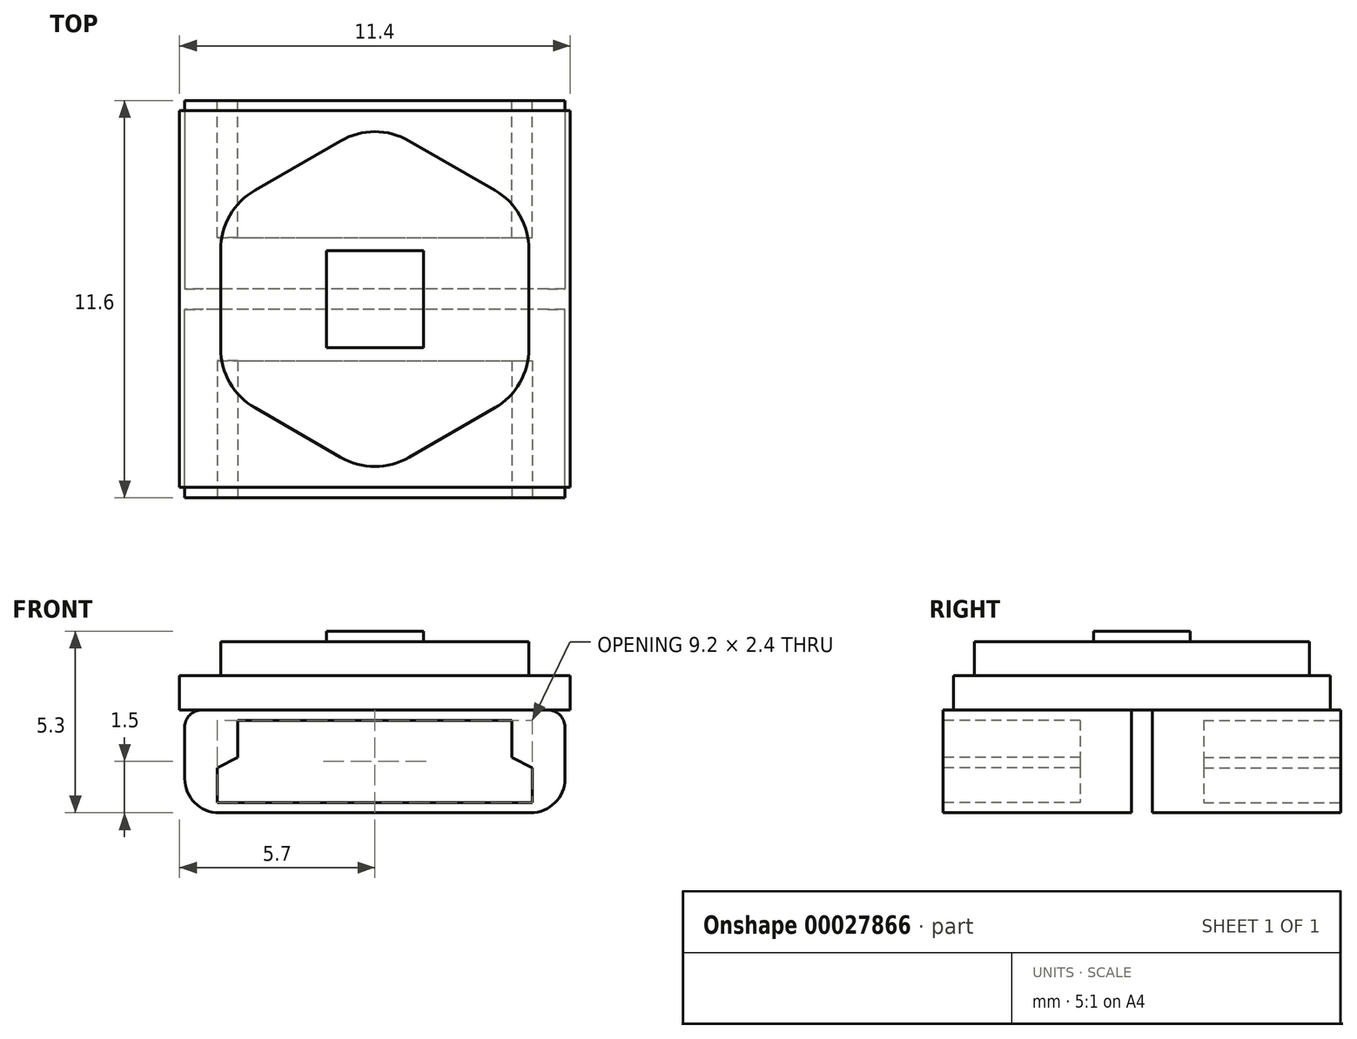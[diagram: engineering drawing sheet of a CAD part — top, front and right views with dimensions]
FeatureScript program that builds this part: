
annotation { "Feature Type Name" : "Feature", "Feature Type Description" : "" }
export const myFeature = defineFeature(function(context is Context, id is Id, definition is map)
    precondition{}
    {
        {
            var Q0;
            Q0=qCreatedBy(makeId("Top.planeOp"),FACE);
            var sketch = newSketch(context, id + "F0", { "sketchPlane" : qUnion([Q0])});
            skLineSegment(sketch, "E0.rect.bottom", {"start": v(6, -6) * mm, "end": v(-6, -6) * mm});
            skLineSegment(sketch, "E0.rect.top", {"start": v(6, 6) * mm, "end": v(-6, 6) * mm});
            skLineSegment(sketch, "E0.rect.left", {"start": v(6, -6) * mm, "end": v(6, 6) * mm});
            skLineSegment(sketch, "E0.rect.right", {"start": v(-6, -6) * mm, "end": v(-6, 6) * mm});
            skPoint(sketch, "E0.rect.middle", {"position": v(0, 0) * mm});
            skCircle(sketch, "E1", {"center": v(0, 0) * mm, "radius": 1.5 * mm});
            skSolve(sketch);
        }
        {
            var Q0;
            Q0=qCreatedBy(makeId("Front.planeOp"),FACE);
            var sketch = newSketch(context, id + "F1", { "sketchPlane" : qUnion([Q0])});
            skLineSegment(sketch, "E2.rect.bottom", {"start": v(6, -6) * mm, "end": v(-6, -6) * mm});
            skLineSegment(sketch, "E2.rect.top", {"start": v(6, 6) * mm, "end": v(-6, 6) * mm});
            skLineSegment(sketch, "E2.rect.left", {"start": v(6, -6) * mm, "end": v(6, 6) * mm});
            skLineSegment(sketch, "E2.rect.right", {"start": v(-6, -6) * mm, "end": v(-6, 6) * mm});
            skPoint(sketch, "E2.rect.middle", {"position": v(0, 0) * mm});
            skCircle(sketch, "E3", {"center": v(0, 0) * mm, "radius": 1.5 * mm});
            skSolve(sketch);
        }
        {
            var Q0;
            Q0=qCreatedBy(makeId("Right.planeOp"),FACE);
            var sketch = newSketch(context, id + "F2", { "sketchPlane" : qUnion([Q0])});
            skLineSegment(sketch, "E4.rect.bottom", {"start": v(6, -6) * mm, "end": v(-6, -6) * mm});
            skLineSegment(sketch, "E4.rect.top", {"start": v(6, 6) * mm, "end": v(-6, 6) * mm});
            skLineSegment(sketch, "E4.rect.left", {"start": v(6, -6) * mm, "end": v(6, 6) * mm});
            skLineSegment(sketch, "E4.rect.right", {"start": v(-6, -6) * mm, "end": v(-6, 6) * mm});
            skPoint(sketch, "E4.rect.middle", {"position": v(0, 0) * mm});
            skCircle(sketch, "E5", {"center": v(0, 0) * mm, "radius": 1.5 * mm});
            skSolve(sketch);
        }
        {
            var Q0;
            Q0=qCreatedBy(makeId("Top.planeOp"),FACE);
            cPlane(context, id + "F3", {"entities" : qUnion([Q0]), "cplaneType" : CPlaneType.OFFSET, "offset" : 3 * mm, "oppositeDirection" : true, "width" : 150 * mm, "height" : 150 * mm});
        }
        {
            var Q0;
            Q0=qCreatedBy(id+"F3.planeOp",FACE);
            var sketch = newSketch(context, id + "F4", { "sketchPlane" : qUnion([Q0])});
            skLineSegment(sketch, "E6.rect.bottom", {"start": v(5.55, -5.8) * mm, "end": v(-5.55, -5.8) * mm});
            skLineSegment(sketch, "E6.rect.top", {"start": v(5.55, -0.3) * mm, "end": v(-5.55, -0.3) * mm});
            skLineSegment(sketch, "E6.rect.left", {"start": v(5.55, -5.8) * mm, "end": v(5.55, -0.3) * mm});
            skLineSegment(sketch, "E6.rect.right", {"start": v(-5.55, -5.8) * mm, "end": v(-5.55, -0.3) * mm});
            skPoint(sketch, "E6.rect.middle", {"position": v(0, -3.05) * mm});
            skSolve(sketch);
        }
        {
            var Q0;
            Q0=makeQuery(id+"F4.imprint","IMPRINT",FACE,{"disambiguationData":[TD([[makeQuery(id+"F4.imprint","IMPRINT",EDGE,{"derivedFrom":sQuery(id+"F4.wireOp",EDGE,"E6.rect.bottom")}),-1.0]])]});
            extrude(context, id + "F5", {"entities" : qUnion([Q0]), "oppositeDirection" : true, "depth" : 3 * mm});
        }
        {
            var Q0;
            Q0=makeQuery(id+"F5.opExtrude","CAP_EDGE",EDGE,{"disambiguationData":[OSD([sQuery(id+"F4.wireOp",EDGE,"E6.rect.right")])],"isStart":false});
            var Q1;
            Q1=makeQuery(id+"F5.opExtrude","CAP_EDGE",EDGE,{"disambiguationData":[OSD([sQuery(id+"F4.wireOp",EDGE,"E6.rect.left")])],"isStart":false});
            fillet(context, id + "F6", {"entities" : qUnion([Q0, Q1]), "radius" : 1 * mm, "tangentPropagation" : true, "allowEdgeOverflow" : false});
        }
        {
            var Q0;
            Q0=makeQuery(id+"F5.opExtrude","SWEPT_FACE",FACE,{"disambiguationData":[OSD([sQuery(id+"F4.wireOp",EDGE,"E6.rect.bottom")])]});
            var sketch = newSketch(context, id + "F7", { "sketchPlane" : qUnion([Q0])});
            skLineSegment(sketch, "E7", {"start": v(0, -3.3) * mm, "end": v(-4, -3.3) * mm});
            skLineSegment(sketch, "E8", {"start": v(-4, -3.3) * mm, "end": v(-4, -4.38) * mm});
            skLineSegment(sketch, "E9", {"start": v(-4, -4.38) * mm, "end": v(-4.6, -4.68) * mm});
            skLineSegment(sketch, "E10", {"start": v(-4.6, -4.68) * mm, "end": v(-4.6, -5.7) * mm});
            skLineSegment(sketch, "E11", {"start": v(-4.6, -5.7) * mm, "end": v(0, -5.7) * mm});
            skLineSegment(sketch, "E12", {"start": v(0, -3.3) * mm, "end": v(0, -5.7) * mm, "construction": true});
            skLineSegment(sketch, "E13.0.MirrorCS", {"start": v(0, -3.3) * mm, "end": v(4, -3.3) * mm});
            skLineSegment(sketch, "E14.0.MirrorCS", {"start": v(4, -3.3) * mm, "end": v(4, -4.38) * mm});
            skLineSegment(sketch, "E15.0.MirrorCS", {"start": v(4, -4.38) * mm, "end": v(4.6, -4.68) * mm});
            skLineSegment(sketch, "E16.0.MirrorCS", {"start": v(4.6, -4.68) * mm, "end": v(4.6, -5.7) * mm});
            skLineSegment(sketch, "E17.0.MirrorCS", {"start": v(4.6, -5.7) * mm, "end": v(0, -5.7) * mm});
            skSolve(sketch);
        }
        {
            var Q0;
            Q0=qSketchRegion(id+"F7",true);
            extrude(context, id + "F8", {"entities" : qUnion([Q0]), "operationType" : NewBodyOperationType.REMOVE, "oppositeDirection" : true, "depth" : 4 * mm});
        }
        {
            var Q0;
            Q0=makeQuery(id+"F5.opExtrude","CAP_EDGE",EDGE,{"disambiguationData":[OSD([sQuery(id+"F4.wireOp",EDGE,"E6.rect.right")])],"isStart":true});
            var Q1;
            Q1=makeQuery(id+"F5.opExtrude","CAP_EDGE",EDGE,{"disambiguationData":[OSD([sQuery(id+"F4.wireOp",EDGE,"E6.rect.left")])],"isStart":true});
            fillet(context, id + "F9", {"entities" : qUnion([Q0, Q1]), "radius" : 0.5 * mm, "tangentPropagation" : true, "allowEdgeOverflow" : false});
        }
        {
            var Q0;
            Q0=makeQuery(id+"F5.opExtrude","SWEPT_BODY",BODY,{"disambiguationData":[OSD([sQuery(id+"F4.wireOp",EDGE,"E6.rect.bottom"),sQuery(id+"F4.wireOp",EDGE,"E6.rect.top"),sQuery(id+"F4.wireOp",EDGE,"E6.rect.left"),sQuery(id+"F4.wireOp",EDGE,"E6.rect.right")])]});
            var Q1;
            Q1=qCreatedBy(makeId("Front.planeOp"),FACE);
            mirror(context, id + "F10", {"entities" : qUnion([Q0]), "mirrorPlane" : qUnion([Q1])});
        }
        {
            var Q0;
            Q0=qCreatedBy(id+"F3.planeOp",FACE);
            var sketch = newSketch(context, id + "F11", { "sketchPlane" : qUnion([Q0])});
            skLineSegment(sketch, "E18.rect.bottom", {"start": v(-5.7, -5.5) * mm, "end": v(5.7, -5.5) * mm});
            skLineSegment(sketch, "E18.rect.top", {"start": v(-5.7, 5.5) * mm, "end": v(5.7, 5.5) * mm});
            skLineSegment(sketch, "E18.rect.left", {"start": v(-5.7, -5.5) * mm, "end": v(-5.7, 5.5) * mm});
            skLineSegment(sketch, "E18.rect.right", {"start": v(5.7, -5.5) * mm, "end": v(5.7, 5.5) * mm});
            skPoint(sketch, "E18.rect.middle", {"position": v(0, 0) * mm});
            skSolve(sketch);
        }
        {
            var Q0;
            Q0=qSketchRegion(id+"F11",true);
            extrude(context, id + "F12", {"entities" : qUnion([Q0]), "depth" : 1 * mm});
        }
        {
            var Q0;
            Q0=qCreatedBy(makeId("Top.planeOp"),FACE);
            cPlane(context, id + "F13", {"entities" : qUnion([Q0]), "cplaneType" : CPlaneType.OFFSET, "offset" : 2 * mm, "oppositeDirection" : true, "width" : 150 * mm, "height" : 150 * mm});
        }
        {
            var Q0;
            Q0=qCreatedBy(id+"F13.planeOp",FACE);
            var sketch = newSketch(context, id + "F14", { "sketchPlane" : qUnion([Q0])});
            skCircle(sketch, "E19.cCircle", {"center": v(0, 0) * mm, "radius": 4.5 * mm, "construction": true});
            skLineSegment(sketch, "E19.0", {"start": v(4.5, -2.6) * mm, "end": v(0, -5.2) * mm});
            skLineSegment(sketch, "E19.1", {"start": v(0, -5.2) * mm, "end": v(-4.5, -2.6) * mm});
            skLineSegment(sketch, "E19.2", {"start": v(-4.5, -2.6) * mm, "end": v(-4.5, 2.6) * mm});
            skLineSegment(sketch, "E19.3", {"start": v(-4.5, 2.6) * mm, "end": v(0, 5.2) * mm});
            skLineSegment(sketch, "E19.4", {"start": v(0, 5.2) * mm, "end": v(4.5, 2.6) * mm});
            skLineSegment(sketch, "E19.5", {"start": v(4.5, 2.6) * mm, "end": v(4.5, -2.6) * mm});
            skPoint(sketch, "E19.0.midPoint", {"position": v(2.25, -3.9) * mm});
            skLineSegment(sketch, "E20.rect.bottom", {"start": v(1.42, -1.42) * mm, "end": v(-1.41, -1.42) * mm});
            skLineSegment(sketch, "E20.rect.top", {"start": v(1.42, 1.42) * mm, "end": v(-1.41, 1.41) * mm});
            skLineSegment(sketch, "E20.rect.left", {"start": v(1.42, -1.42) * mm, "end": v(1.42, 1.42) * mm});
            skLineSegment(sketch, "E20.rect.right", {"start": v(-1.42, -1.42) * mm, "end": v(-1.41, 1.41) * mm});
            skSolve(sketch);
        }
        {
            var Q0;
            Q0=qCreatedBy(id+"F13.planeOp",FACE);
            var sketch = newSketch(context, id + "F15", { "sketchPlane" : qUnion([Q0])});
            skLineSegment(sketch, "E21.0", {"start": v(-3.5, 3.18) * mm, "end": v(-1, 4.62) * mm});
            skLineSegment(sketch, "E21.1", {"start": v(-4.5, -1.44) * mm, "end": v(-4.5, 1.44) * mm});
            skLineSegment(sketch, "E21.2", {"start": v(-1, -4.62) * mm, "end": v(-3.5, -3.18) * mm});
            skLineSegment(sketch, "E21.3", {"start": v(3.5, -3.18) * mm, "end": v(1, -4.62) * mm});
            skLineSegment(sketch, "E21.4", {"start": v(4.5, 1.44) * mm, "end": v(4.5, -1.44) * mm});
            skLineSegment(sketch, "E21.5", {"start": v(1, 4.62) * mm, "end": v(3.5, 3.18) * mm});
            skPoint(sketch, "E22.visualSharp", {"position": v(0, 5.2) * mm});
            skArc(sketch, "E22.filletArc", {"start": v(1, 4.62) * mm, "mid": v(0, 4.89) * mm, "end": v(-1, 4.62) * mm});
            skPoint(sketch, "E23.visualSharp", {"position": v(-4.5, 2.6) * mm});
            skArc(sketch, "E23.filletArc", {"start": v(-3.5, 3.18) * mm, "mid": v(-4.23, 2.44) * mm, "end": v(-4.5, 1.44) * mm});
            skPoint(sketch, "E24.visualSharp", {"position": v(4.5, 2.6) * mm});
            skArc(sketch, "E24.filletArc", {"start": v(4.5, 1.44) * mm, "mid": v(4.23, 2.44) * mm, "end": v(3.5, 3.18) * mm});
            skPoint(sketch, "E25.visualSharp", {"position": v(4.5, -2.6) * mm});
            skArc(sketch, "E25.filletArc", {"start": v(3.5, -3.18) * mm, "mid": v(4.23, -2.44) * mm, "end": v(4.5, -1.44) * mm});
            skPoint(sketch, "E26.visualSharp", {"position": v(0, -5.2) * mm});
            skArc(sketch, "E26.filletArc", {"start": v(-1, -4.62) * mm, "mid": v(0, -4.89) * mm, "end": v(1, -4.62) * mm});
            skPoint(sketch, "E27.visualSharp", {"position": v(-4.5, -2.6) * mm});
            skArc(sketch, "E27.filletArc", {"start": v(-4.5, -1.44) * mm, "mid": v(-4.23, -2.44) * mm, "end": v(-3.5, -3.18) * mm});
            skSolve(sketch);
        }
        {
            var Q0;
            Q0=qSketchRegion(id+"F15",true);
            extrude(context, id + "F16", {"entities" : qUnion([Q0]), "depth" : 1 * mm});
        }
        {
            var Q0;
            Q0=makeQuery(id+"F16.opExtrude","CAP_FACE",FACE,{"disambiguationData":[OSD([sQuery(id+"F15.wireOp",EDGE,"E21.0"),sQuery(id+"F15.wireOp",EDGE,"E21.1"),sQuery(id+"F15.wireOp",EDGE,"E21.2"),sQuery(id+"F15.wireOp",EDGE,"E21.3"),sQuery(id+"F15.wireOp",EDGE,"E21.4"),sQuery(id+"F15.wireOp",EDGE,"E21.5"),sQuery(id+"F15.wireOp",EDGE,"E22.filletArc"),sQuery(id+"F15.wireOp",EDGE,"E23.filletArc"),sQuery(id+"F15.wireOp",EDGE,"E24.filletArc"),sQuery(id+"F15.wireOp",EDGE,"E25.filletArc"),sQuery(id+"F15.wireOp",EDGE,"E26.filletArc"),sQuery(id+"F15.wireOp",EDGE,"E27.filletArc")])],"isStart":false});
            var sketch = newSketch(context, id + "F17", { "sketchPlane" : qUnion([Q0])});
            skLineSegment(sketch, "E28.0", {"start": v(1.42, 1.42) * mm, "end": v(-1.41, 1.41) * mm});
            skLineSegment(sketch, "E28.1", {"start": v(-1.42, -1.42) * mm, "end": v(-1.41, 1.41) * mm});
            skLineSegment(sketch, "E28.2", {"start": v(1.42, -1.42) * mm, "end": v(-1.41, -1.42) * mm});
            skLineSegment(sketch, "E28.3", {"start": v(1.42, -1.42) * mm, "end": v(1.42, 1.42) * mm});
            skSolve(sketch);
        }
        {
            var Q0;
            Q0=qSketchRegion(id+"F17",true);
            extrude(context, id + "F18", {"entities" : qUnion([Q0]), "depth" : 0.3 * mm});
        }
    });
